# Revit family: Wave Desk - LH
name_source: partatom
category: Furniture
units: mm (PartAtom-declared; Revit-internal decimal feet)

## family parameters
Always vertical = Yes
Cut with Voids When Loaded = No
OmniClass Number = 23.40.20.00
OmniClass Title = General Furniture and Specialties
Room Calculation Point = No
Shared = No
Work Plane-Based = No

## types (4) — shared parameters
Assembly Code = E2020200
Desktop = Gresham - Midnight Ash
Foot = Gresham - Black Plastic
Frame = Gresham - Silver Metal
Manufacturer = Gresham Office Furniture
Range = RISE
URL = www.gof.co.uk

## per-type parameters (varying)
| type | Product Code | Width |
| 1600 x 800 x 1000 | HDWL16 | 1600 mm  [stored 5.24934 ft] |
| 1800 x 800 x 1000 | HDWL18 | 1800 mm  [stored 5.90551 ft] |
| 1400 x 800 x 1000 | HDWL14 | 1400 mm  [stored 4.59318 ft] |
| 1200 x 800 x 1000 | HDWL12 | 1200 mm |

note: [stored X ft] marks values corroborated as IEEE doubles in the binary element streams (Revit-internal decimal feet)

## geometry (parser evidence)
native form markers: Sweep x13
no freeform markers — native parametric forms only
